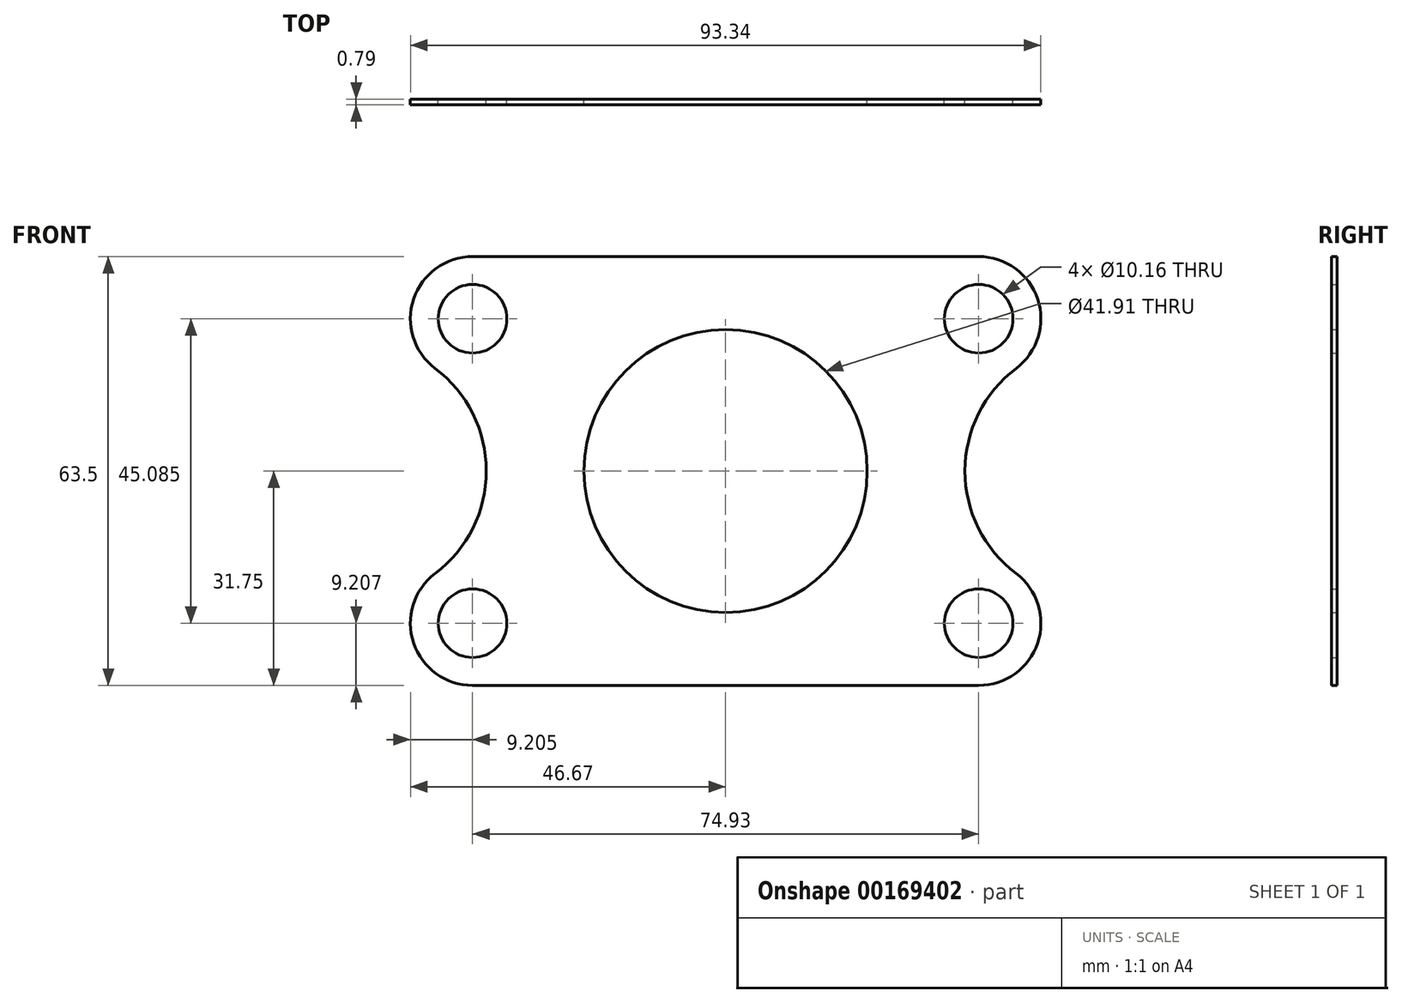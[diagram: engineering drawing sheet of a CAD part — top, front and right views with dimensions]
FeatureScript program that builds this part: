
annotation { "Feature Type Name" : "Feature", "Feature Type Description" : "" }
export const myFeature = defineFeature(function(context is Context, id is Id, definition is map)
    precondition{}
    {
        {
            var Q0;
            Q0=qCreatedBy(makeId("Front.planeOp"),FACE);
            var sketch = newSketch(context, id + "F0", { "sketchPlane" : qUnion([Q0])});
            skLineSegment(sketch, "E0.bottom", {"start": v(-37.47, 31.75) * mm, "end": v(37.46, 31.75) * mm});
            skLineSegment(sketch, "E0.top", {"start": v(-37.46, -31.75) * mm, "end": v(37.47, -31.75) * mm});
            skPoint(sketch, "E0.middle", {"position": v(0, 0) * mm});
            skCircle(sketch, "E1", {"center": v(-37.46, 22.54) * mm, "radius": 5.08 * mm});
            skCircle(sketch, "E2", {"center": v(37.46, 22.54) * mm, "radius": 5.08 * mm});
            skCircle(sketch, "E3", {"center": v(37.46, -22.54) * mm, "radius": 5.08 * mm});
            skCircle(sketch, "E4", {"center": v(-37.46, -22.54) * mm, "radius": 5.08 * mm});
            skLineSegment(sketch, "E5.bottom", {"start": v(-37.46, 22.54) * mm, "end": v(37.46, 22.54) * mm, "construction": true});
            skLineSegment(sketch, "E5.top", {"start": v(-37.46, -22.54) * mm, "end": v(37.46, -22.54) * mm, "construction": true});
            skLineSegment(sketch, "E5.left", {"start": v(-37.46, 22.54) * mm, "end": v(-37.46, -22.54) * mm, "construction": true});
            skLineSegment(sketch, "E5.right", {"start": v(37.46, 22.54) * mm, "end": v(37.46, -22.54) * mm, "construction": true});
            skLineSegment(sketch, "E6", {"start": v(-35.43, 0) * mm, "end": v(35.43, 0) * mm, "construction": true});
            skPoint(sketch, "E7.visualSharp", {"position": v(-46.67, 31.75) * mm});
            skArc(sketch, "E7.filletArc", {"start": v(-37.47, 31.75) * mm, "mid": v(-43.98, 29.05) * mm, "end": v(-46.67, 22.54) * mm});
            skPoint(sketch, "E8.visualSharp", {"position": v(46.67, 31.75) * mm});
            skArc(sketch, "E8.filletArc", {"start": v(46.67, 22.54) * mm, "mid": v(43.98, 29.05) * mm, "end": v(37.46, 31.75) * mm});
            skPoint(sketch, "E9.visualSharp", {"position": v(46.67, -31.75) * mm});
            skArc(sketch, "E9.filletArc", {"start": v(37.47, -31.75) * mm, "mid": v(43.98, -29.05) * mm, "end": v(46.67, -22.54) * mm});
            skPoint(sketch, "E10.visualSharp", {"position": v(-46.67, -31.75) * mm});
            skArc(sketch, "E10.filletArc", {"start": v(-46.67, -22.54) * mm, "mid": v(-43.98, -29.05) * mm, "end": v(-37.46, -31.75) * mm});
            skCircle(sketch, "E11", {"center": v(0, 0) * mm, "radius": 20.96 * mm});
            skArc(sketch, "E12", {"start": v(-43, -15.19) * mm, "mid": v(-35.43, 0) * mm, "end": v(-43, 15.19) * mm});
            skArc(sketch, "E13", {"start": v(-37.47, 31.75) * mm, "mid": v(-46.2, 25.46) * mm, "end": v(-43, 15.19) * mm});
            skArc(sketch, "E14", {"start": v(-43, -15.19) * mm, "mid": v(-46.2, -25.46) * mm, "end": v(-37.46, -31.75) * mm});
            skArc(sketch, "E15", {"start": v(43, 15.19) * mm, "mid": v(46.2, 25.46) * mm, "end": v(37.46, 31.75) * mm});
            skArc(sketch, "E16", {"start": v(37.47, -31.75) * mm, "mid": v(46.2, -25.46) * mm, "end": v(43, -15.19) * mm});
            skArc(sketch, "E17", {"start": v(43, 15.19) * mm, "mid": v(35.43, 0) * mm, "end": v(43, -15.19) * mm});
            skSolve(sketch);
        }
        {
            var Q0;
            Q0 = qSketchRegion(id + "F0", true);
            extrude(context, id + "F1", {"entities" : qUnion([Q0]), "depth" : 0.8 * mm});
        }
    });
